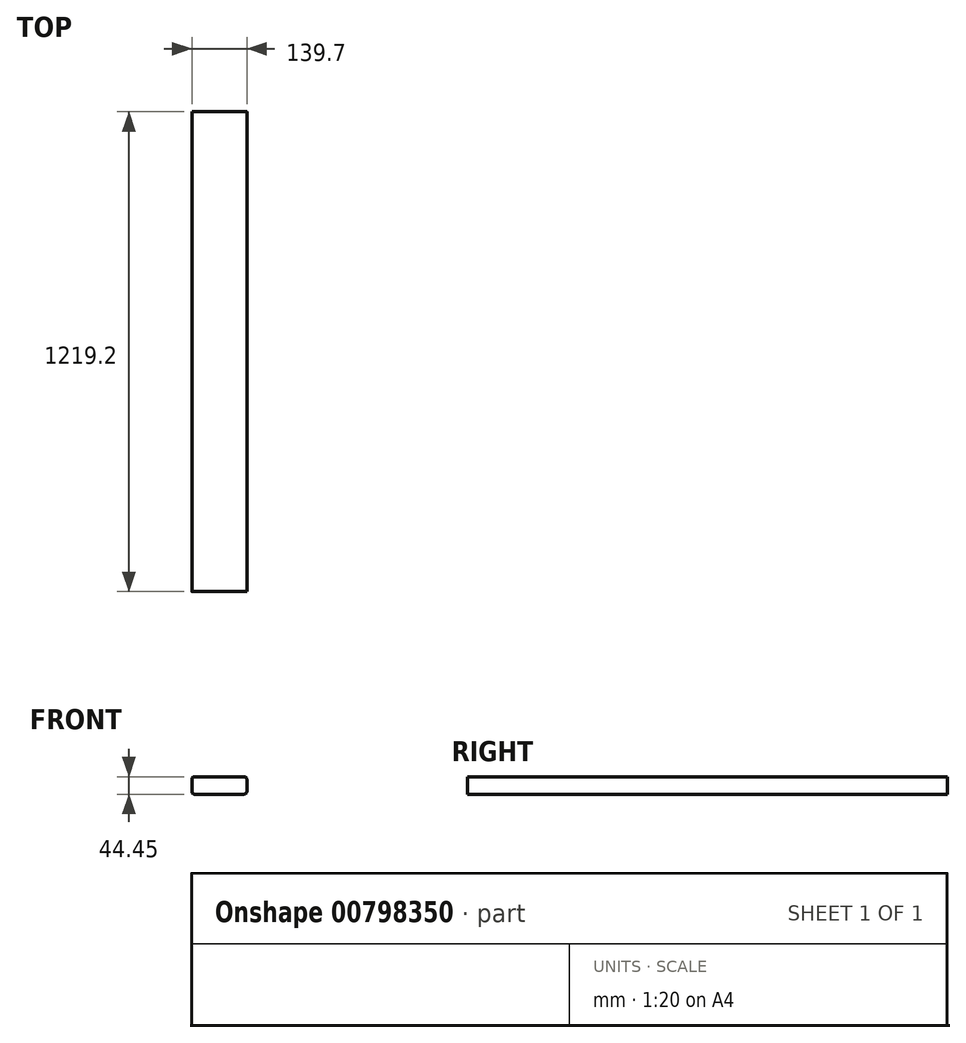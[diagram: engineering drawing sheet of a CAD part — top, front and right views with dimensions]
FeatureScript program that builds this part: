
annotation { "Feature Type Name" : "Feature", "Feature Type Description" : "" }
export const myFeature = defineFeature(function(context is Context, id is Id, definition is map)
    precondition{}
    {
        {
            var Q0;
            Q0=qCreatedBy(makeId("Front.planeOp"),FACE);
            var sketch = newSketch(context, id + "F0", { "sketchPlane" : qUnion([Q0])});
            skLineSegment(sketch, "E0.bottom", {"start": v(6.35, 0) * mm, "end": v(133.35, 0) * mm});
            skLineSegment(sketch, "E0.top", {"start": v(6.35, 44.45) * mm, "end": v(133.35, 44.45) * mm});
            skLineSegment(sketch, "E0.left", {"start": v(0, 6.35) * mm, "end": v(0, 38.1) * mm});
            skLineSegment(sketch, "E0.right", {"start": v(139.7, 6.35) * mm, "end": v(139.7, 38.1) * mm});
            skPoint(sketch, "E1.visualSharp", {"position": v(0, 44.45) * mm});
            skArc(sketch, "E1.filletArc", {"start": v(6.35, 44.45) * mm, "mid": v(1.86, 42.6) * mm, "end": v(0, 38.1) * mm});
            skPoint(sketch, "E2.visualSharp", {"position": v(0, 0) * mm});
            skArc(sketch, "E2.filletArc", {"start": v(0, 6.35) * mm, "mid": v(1.86, 1.86) * mm, "end": v(6.35, 0) * mm});
            skPoint(sketch, "E3.visualSharp", {"position": v(139.7, 0) * mm});
            skArc(sketch, "E3.filletArc", {"start": v(133.35, 0) * mm, "mid": v(137.84, 1.86) * mm, "end": v(139.7, 6.35) * mm});
            skPoint(sketch, "E4.visualSharp", {"position": v(139.7, 44.45) * mm});
            skArc(sketch, "E4.filletArc", {"start": v(139.7, 38.1) * mm, "mid": v(137.84, 42.6) * mm, "end": v(133.35, 44.45) * mm});
            skSolve(sketch);
        }
        {
            var Q0;
            Q0=makeQuery(id+"F0.imprint","IMPRINT",FACE,{"disambiguationData":[TD([[makeQuery(id+"F0.imprint","IMPRINT",EDGE,{"derivedFrom":sQuery(id+"F0.wireOp",EDGE,"E0.bottom")}),1.0]])]});
            extrude(context, id + "F1", {"entities" : qUnion([Q0]), "depth" : 1219.2 * mm, "offsetDistance" : 25.4 * mm});
        }
    });
